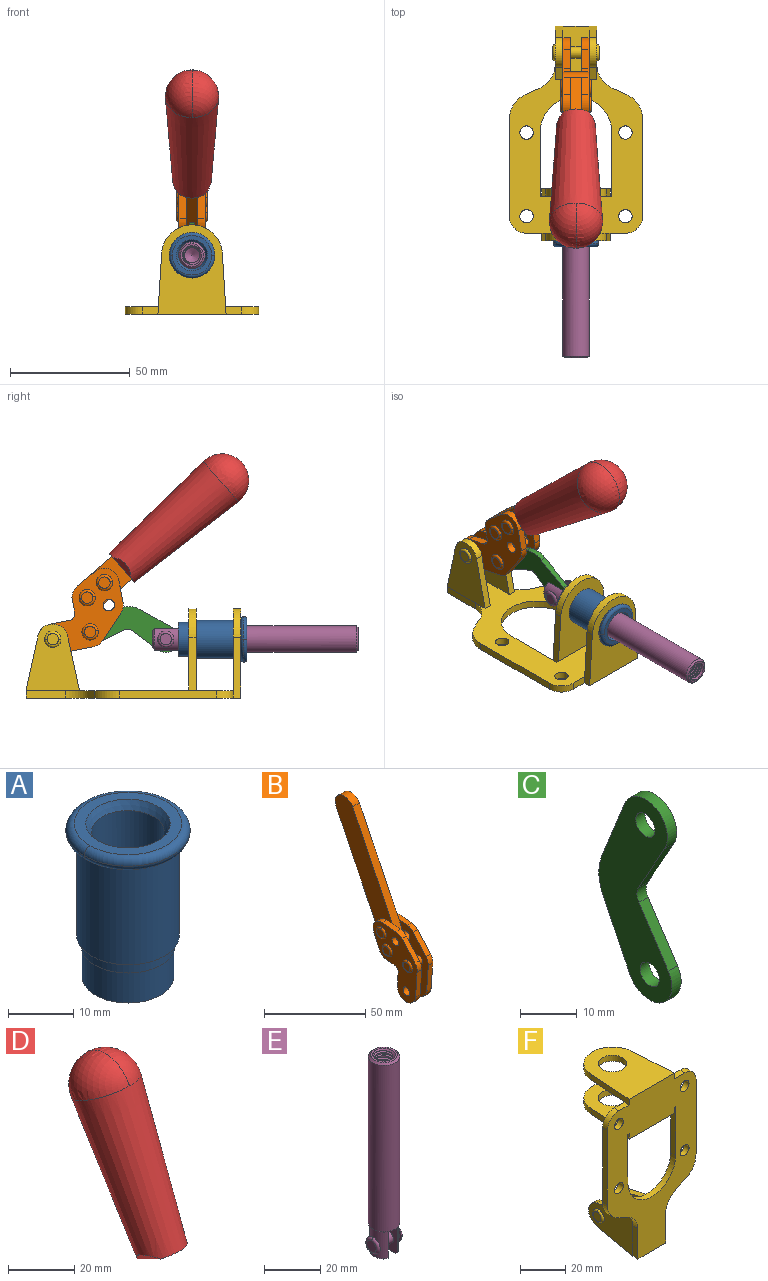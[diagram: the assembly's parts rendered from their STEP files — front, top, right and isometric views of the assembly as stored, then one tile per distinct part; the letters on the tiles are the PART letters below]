
ASSEMBLY  parts=6 mates=6
PART A: 15 faces, bbox 20.6x20.6x28.7 mm
  f0: torus R=8.26mm, axis (0,0,1), area 56.8mm2, adj f1,f10,f12
  f1: torus R=8.26mm, axis (0,0,1), area 56.8mm2, adj f0,f6,f13
  f2: cylinder r=5.59mm len=25.91mm, axis (0,0,1), area 909.6mm2, adj f3,f4
  f3: cone r=6.86mm half-angle=45deg, axis (0,0,-1), area 70.2mm2, adj f2,f14
  f4: cone r=6.47mm half-angle=30deg, axis (0,0,1), area 66.7mm2, adj f2,f13
  f5: cylinder r=7.04mm len=14.07mm, axis (0,0,1), area 252.6mm2, adj f11,f14
  f6: torus R=8.26mm, axis (0,0,1), area 56.8mm2, adj f1,f12,f13
  f7: cylinder r=7.16mm len=14.33mm, axis (0,0,1), area 91.5mm2, adj f9,f11
  f8: cylinder r=7.86mm len=18.42mm, axis (0,0,1), area 909.6mm2, adj f9,f10
  f9: plane 15.72x15.72mm, normal (0,0,-1), area 33mm2, adj f7,f8
  f10: plane 16.51x16.51mm, normal (0,0,-1), area 19.9mm2, adj f0,f8,f12
  f11: plane 14.33x14.33mm, normal (0,0,-1), area 5.7mm2, adj f5,f7
  f12: torus R=8.26mm, axis (0,0,1), area 56.8mm2, adj f0,f6,f10
  f13: plane 16.51x16.51mm, normal (0,0,1), area 82.7mm2, adj f1,f4,f6
  f14: plane 14.07x14.07mm, normal (0,0,-1), area 7.8mm2, adj f3,f5
PART B: 59 faces, bbox 12.9x60.2x99.6 mm
  f0: torus R=2.39mm, axis (-1,0,0), area 14.9mm2, adj f20,f43,f51
  f1: torus R=2.39mm, axis (-1,0,0), area 14.9mm2, adj f19,f42,f51
  f2: torus R=2.39mm, axis (-1,0,0), area 14.9mm2, adj f18,f35,f51
  f3: torus R=2.39mm, axis (-1,0,0), area 14.9mm2, adj f14,f17,f23
  f4: torus R=2.39mm, axis (-1,0,0), area 14.9mm2, adj f13,f16,f23
  f5: torus R=2.39mm, axis (-1,0,0), area 14.9mm2, adj f12,f15,f23
  f6: cylinder r=2.39mm len=4.78mm, axis (1,0,0), area 46.5mm2, adj f48,f50,f51
  f7: cylinder r=2.39mm len=4.78mm, axis (1,0,0), area 46.5mm2, adj f50,f51
  f8: cylinder r=6.35mm len=12.68mm, axis (1,0,0), area 61.8mm2, adj f38,f39,f50,f51
  f9: cylinder r=2.39mm len=4.78mm, axis (-1,0,0), area 70.5mm2, adj f46,f50
  f10: cylinder r=2.39mm len=4.78mm, axis (-1,0,0), area 46.5mm2, adj f23,f45,f46
  f11: cylinder r=2.39mm len=4.78mm, axis (-1,0,0), area 46.5mm2, adj f23,f46
  f12: plane 4.78x4.78mm, normal (1,0,0), area 17.9mm2, adj f5,f15
  f13: plane 4.78x4.78mm, normal (1,0,0), area 17.9mm2, adj f4,f16
  f14: plane 4.78x4.78mm, normal (1,0,0), area 17.9mm2, adj f3,f17
  f15: torus R=2.39mm, axis (-1,0,0), area 14.9mm2, adj f5,f12,f23
  f16: torus R=2.39mm, axis (-1,0,0), area 14.9mm2, adj f4,f13,f23
  f17: torus R=2.39mm, axis (-1,0,0), area 14.9mm2, adj f3,f14,f23
  f18: plane 4.78x4.78mm, normal (-1,0,0), area 17.9mm2, adj f2,f35
  f19: plane 4.78x4.78mm, normal (-1,0,0), area 17.9mm2, adj f1,f42
  f20: plane 4.78x4.78mm, normal (-1,0,0), area 17.9mm2, adj f0,f43
  f21: plane 2.26x0.2mm, normal (1,0,0), area 0.2mm2, adj f31,f44
  f22: plane 2.26x0.2mm, normal (-1,0,0), area 0.2mm2, adj f41,f44
  f23: plane 39.37x30.77mm, normal (1,0,0), area 565.5mm2, adj f3,f4,f5,f10,f11,f15,f16,f17
  f24: cylinder r=6.1mm len=4.15mm, axis (-1,0,0), area 14.7mm2, adj f23,f25,f32,f46
  f25: plane 10.25x9.01mm, normal (0,-0.75,0.66), area 42.3mm2, adj f23,f24,f26,f46
  f26: cylinder r=6.35mm len=4.64mm, axis (-1,0,0), area 15.6mm2, adj f23,f25,f27,f46
  f27: plane 15.84x3.1mm, normal (0,-1,-0.07), area 49.2mm2, adj f23,f26,f28,f46
  f28: cylinder r=6.35mm len=12.68mm, axis (-1,0,0), area 61.8mm2, adj f23,f27,f29,f46
  f29: plane 8.11x3.1mm, normal (0,1,0.07), area 25.2mm2, adj f23,f28,f30,f46
  f30: cylinder r=3.05mm len=3.25mm, axis (-1,0,0), area 14.8mm2, adj f23,f29,f31,f46
  f31: plane 5.99x3.1mm, normal (0,0.07,-1), area 18.6mm2, adj f21,f23,f30,f44,f46
  f32: plane 9.5x3.1mm, normal (0,-0.07,1), area 29.5mm2, adj f23,f24,f33,f46,f47
  f33: cylinder r=6.1mm len=8.63mm, axis (-1,0,0), area 39.1mm2, adj f23,f32,f34,f47
  f34: plane 8.65x3.96mm, normal (0,0.91,-0.42), area 29.5mm2, adj f23,f33,f44,f47
  f35: torus R=2.39mm, axis (-1,0,0), area 14.9mm2, adj f2,f18,f51
  f36: plane 10.25x9.01mm, normal (0,-0.75,0.66), area 42.3mm2, adj f37,f49,f50,f51
  f37: cylinder r=6.35mm len=4.64mm, axis (1,0,0), area 15.6mm2, adj f36,f38,f50,f51
  f38: plane 15.84x3.1mm, normal (0,-1,-0.07), area 49.2mm2, adj f8,f37,f50,f51
  f39: plane 8.11x3.1mm, normal (0,1,0.07), area 25.2mm2, adj f8,f40,f50,f51
  f40: cylinder r=3.05mm len=3.25mm, axis (1,0,0), area 14.8mm2, adj f39,f41,f50,f51
  f41: plane 5.99x3.1mm, normal (0,0.07,-1), area 18.6mm2, adj f22,f40,f44,f50,f51
  f42: torus R=2.39mm, axis (-1,0,0), area 14.9mm2, adj f1,f19,f51
  f43: torus R=2.39mm, axis (-1,0,0), area 14.9mm2, adj f0,f20,f51
  f44: cylinder r=6.35mm len=12.12mm, axis (-1,0,0), area 128.9mm2, adj f21,f22,f23,f31,f34,f41,f46,f47
  f45: plane 2.65x1.35mm, normal (1,0,0), area 1mm2, adj f10,f55
  f46: plane 39.08x20.42mm, normal (-1,0,0), area 412.5mm2, adj f9,f10,f11,f24,f25,f26,f27,f28
  f47: plane 77.62x39.82mm, normal (1,0,0), area 850mm2, adj f32,f33,f34,f44,f53,f54,f55
  f48: plane 2.65x1.35mm, normal (-1,0,0), area 1mm2, adj f6,f55
  f49: cylinder r=6.1mm len=4.15mm, axis (1,0,0), area 14.7mm2, adj f36,f50,f51,f56
  f50: plane 39.08x20.42mm, normal (1,0,0), area 412.5mm2, adj f6,f7,f8,f9,f36,f37,f38,f39
  f51: plane 39.37x30.77mm, normal (-1,0,0), area 565.5mm2, adj f0,f1,f2,f6,f7,f8,f35,f36
  f52: plane 8.65x3.96mm, normal (0,0.91,-0.42), area 29.5mm2, adj f44,f51,f57,f58
  f53: plane 68.49x33.4mm, normal (0,0.9,-0.44), area 358.1mm2, adj f44,f47,f54,f58
  f54: cylinder r=6.35mm len=12.06mm, axis (1,0,0), area 93.7mm2, adj f47,f53,f55,f58
  f55: plane 68.49x33.4mm, normal (0,-0.9,0.44), area 358.1mm2, adj f44,f45,f46,f47,f48,f50,f54,f58
  f56: plane 9.5x3.1mm, normal (0,-0.07,1), area 29.5mm2, adj f49,f50,f51,f57,f58
  f57: cylinder r=6.1mm len=8.63mm, axis (1,0,0), area 39.1mm2, adj f51,f52,f56,f58
  f58: plane 77.62x39.82mm, normal (-1,0,0), area 850mm2, adj f44,f52,f53,f54,f55,f56,f57
PART C: 12 faces, bbox 2.3x18.2x42.8 mm
  f0: cylinder r=2.4mm len=4.8mm, axis (1,0,0), area 34.9mm2, adj f4,f11
  f1: cylinder r=10.41mm len=8.47mm, axis (1,0,0), area 20.2mm2, adj f4,f9,f10,f11
  f2: cylinder r=3.05mm len=3.16mm, axis (1,0,0), area 7.7mm2, adj f4,f6,f7,f11
  f3: cylinder r=2.4mm len=4.8mm, axis (1,0,0), area 34.9mm2, adj f4,f11
  f4: plane 42.81x18.23mm, normal (-1,0,0), area 414.1mm2, adj f0,f1,f2,f3,f5,f6,f7,f8
  f5: cylinder r=5.54mm len=10.67mm, axis (1,0,0), area 41.8mm2, adj f4,f6,f10,f11
  f6: plane 11.66x6.53mm, normal (0,-0.87,-0.49), area 30.9mm2, adj f2,f4,f5,f11
  f7: plane 11.17x7.33mm, normal (0,-0.84,0.55), area 30.9mm2, adj f2,f4,f8,f11
  f8: cylinder r=5.54mm len=10.51mm, axis (1,0,0), area 41.8mm2, adj f4,f7,f9,f11
  f9: plane 13.67x6.67mm, normal (0,0.9,-0.44), area 35.1mm2, adj f1,f4,f8,f11
  f10: plane 14.1x5.7mm, normal (0,0.93,0.37), area 35.1mm2, adj f1,f4,f5,f11
  f11: plane 42.81x18.23mm, normal (1,0,0), area 414.1mm2, adj f0,f1,f2,f3,f5,f6,f7,f8
PART D: 11 faces, bbox 22.3x42.6x64.5 mm
  f0: sphere r=11.13mm, area 411.4mm2, adj f1,f8
  f1: cone r=11.11mm half-angle=3.3deg, axis (0,0.44,0.9), area 3251.8mm2, adj f0,f7,f8,f9,f10
  f2: cylinder r=6.16mm len=11.7mm, axis (1,0,0), area 89.5mm2, adj f3,f4,f5,f6
  f3: plane 60.23x36.75mm, normal (-1,0,0), area 763.6mm2, adj f2,f4,f6,f10
  f4: plane 51.37x25.05mm, normal (0,0.9,-0.44), area 264.2mm2, adj f2,f3,f5,f10
  f5: plane 60.23x36.75mm, normal (1,0,0), area 763.6mm2, adj f2,f4,f6,f10
  f6: plane 51.37x25.05mm, normal (0,-0.9,0.44), area 264.2mm2, adj f2,f3,f5,f10
  f7: plane 9.95x5.95mm, normal (0.71,-0.31,-0.64), area 25.8mm2, adj f1,f10
  f8: sphere r=11.13mm, area 411.4mm2, adj f0,f1
  f9: plane 9.95x5.95mm, normal (-0.71,-0.31,-0.64), area 25.8mm2, adj f1,f10
  f10: plane 14.27x11.38mm, normal (0,-0.44,-0.9), area 106.7mm2, adj f1,f3,f4,f5,f6,f7,f9
PART E: 48 faces, bbox 12.6x11.1x86.1 mm
  f0: torus R=2.41mm, axis (-1,0,0), area 15mm2, adj f30,f32,f34
  f1: torus R=2.41mm, axis (-1,0,0), area 15mm2, adj f29,f31,f33
  f2: cylinder r=5.54mm len=72.39mm, axis (0,0,1), area 2518.5mm2, adj f3,f4,f42,f43
  f3: cone r=5.54mm half-angle=45deg, axis (0,0,1), area 7.6mm2, adj f2,f5,f41
  f4: cone r=5.54mm half-angle=45deg, axis (0,0,-1), area 34.9mm2, adj f2,f39
  f5: cylinder r=5.08mm len=11.48mm, axis (0,0,1), area 108.3mm2, adj f3,f7,f8,f41
  f6: cylinder r=2.41mm len=4.83mm, axis (-1,0,0), area 71.2mm2, adj f40,f41
  f7: cylinder r=2.41mm len=4.83mm, axis (-1,0,0), area 7.6mm2, adj f5,f34
  f8: cone r=5.08mm half-angle=45deg, axis (0,0,1), area 10.6mm2, adj f5,f37,f41
  f9: cone r=3.98mm half-angle=45deg, axis (0,0,1), area 17.6mm2, adj f27,f39,f45,f46,f47
  f10: cylinder r=2.41mm len=4.83mm, axis (-1,0,0), area 7.6mm2, adj f33,f38
  f11: cylinder r=3.2mm len=6.4mm, axis (0,0,1), area 78.4mm2, adj f12,f28,f44,f45,f47
  f12: cylinder r=3.2mm len=6.4mm, axis (0,0,1), area 10.5mm2, adj f11,f13,f45,f47
  f13: cylinder r=3.2mm len=6.4mm, axis (0,0,1), area 10.5mm2, adj f12,f14,f45,f47
  f14: cylinder r=3.2mm len=6.4mm, axis (0,0,1), area 10.5mm2, adj f13,f15,f45,f47
  f15: cylinder r=3.2mm len=6.4mm, axis (0,0,1), area 10.5mm2, adj f14,f16,f45,f47
  f16: cylinder r=3.2mm len=6.4mm, axis (0,0,1), area 10.5mm2, adj f15,f17,f45,f47
  f17: cylinder r=3.2mm len=6.4mm, axis (0,0,1), area 10.5mm2, adj f16,f18,f45,f47
  f18: cylinder r=3.2mm len=6.4mm, axis (0,0,1), area 10.5mm2, adj f17,f19,f45,f47
  f19: cylinder r=3.2mm len=6.4mm, axis (0,0,1), area 10.5mm2, adj f18,f20,f45,f47
  f20: cylinder r=3.2mm len=6.4mm, axis (0,0,1), area 10.5mm2, adj f19,f21,f45,f47
  f21: cylinder r=3.2mm len=6.4mm, axis (0,0,1), area 10.5mm2, adj f20,f22,f45,f47
  f22: cylinder r=3.2mm len=6.4mm, axis (0,0,1), area 10.5mm2, adj f21,f23,f45,f47
  f23: cylinder r=3.2mm len=6.4mm, axis (0,0,1), area 10.5mm2, adj f22,f24,f45,f47
  f24: cylinder r=3.2mm len=6.4mm, axis (0,0,1), area 10.5mm2, adj f23,f25,f45,f47
  f25: cylinder r=3.2mm len=6.4mm, axis (0,0,1), area 10.5mm2, adj f24,f26,f45,f47
  f26: cylinder r=3.2mm len=6.4mm, axis (0,0,1), area 10.5mm2, adj f25,f27,f45,f47
  f27: cylinder r=3.2mm len=6.4mm, axis (0,0,1), area 7.4mm2, adj f9,f26,f45,f47
  f28: cone r=3.2mm half-angle=60deg, axis (0,0,1), area 37.2mm2, adj f11
  f29: plane 4.83x4.83mm, normal (-1,0,0), area 18.3mm2, adj f1,f31
  f30: plane 4.83x4.83mm, normal (1,0,0), area 18.3mm2, adj f0,f32
  f31: torus R=2.41mm, axis (-1,0,0), area 15mm2, adj f1,f29,f33
  f32: torus R=2.41mm, axis (-1,0,0), area 15mm2, adj f0,f30,f34
  f33: plane 6.83x6.83mm, normal (1,0,0), area 18.3mm2, adj f1,f10,f31
  f34: plane 6.83x6.83mm, normal (-1,0,0), area 18.3mm2, adj f0,f7,f32
  f35: cone r=5.08mm half-angle=45deg, axis (0,0,1), area 10.6mm2, adj f36,f38,f40
  f36: plane 7.25x1.97mm, normal (0,0,-1), area 10mm2, adj f35,f40
  f37: plane 7.25x1.97mm, normal (0,0,-1), area 10mm2, adj f8,f41
  f38: cylinder r=5.08mm len=11.48mm, axis (0,0,1), area 108.3mm2, adj f10,f35,f40,f42
  f39: plane 9.55x9.55mm, normal (0,0,1), area 22mm2, adj f4,f9
  f40: plane 12.76x10.09mm, normal (1,0,0), area 95.7mm2, adj f6,f35,f36,f38,f42,f43
  f41: plane 12.76x10.09mm, normal (-1,0,0), area 95.7mm2, adj f3,f5,f6,f8,f37,f43
  f42: cone r=5.54mm half-angle=45deg, axis (0,0,1), area 7.6mm2, adj f2,f38,f40
  f43: plane 11.07x4.7mm, normal (0,0,-1), area 50.4mm2, adj f2,f40,f41
  f44: plane 0.89x0.62mm, normal (-1,0,0), area 0.3mm2, adj f11,f45,f46,f47
  f45: bspline ~24.8x7.63mm, area 266.6mm2, adj f9,f11,f12,f13,f14,f15,f16,f17
  f46: bspline ~24.87x7.63mm, area 73.6mm2, adj f9,f44,f45,f47
  f47: bspline ~24.98x7.63mm, area 272.5mm2, adj f9,f11,f12,f13,f14,f15,f16,f17
PART F: 55 faces, bbox 55.7x37.4x89.8 mm
  f0: torus R=2.41mm, axis (-1,0,0), area 15mm2, adj f11,f15,f25
  f1: torus R=2.41mm, axis (-1,0,0), area 15mm2, adj f10,f12,f22
  f2: cylinder r=2.78mm len=5.56mm, axis (0,-1,0), area 54.2mm2, adj f30,f54
  f3: cylinder r=14.99mm len=29.97mm, axis (0,-1,0), area 145.9mm2, adj f30,f49,f53,f54
  f4: cylinder r=2.78mm len=5.56mm, axis (0,-1,0), area 54.2mm2, adj f30,f54
  f5: cylinder r=2.78mm len=5.56mm, axis (0,-1,0), area 54.2mm2, adj f30,f54
  f6: cylinder r=2.78mm len=5.56mm, axis (0,-1,0), area 54.2mm2, adj f30,f54
  f7: cylinder r=6.35mm len=12.7mm, axis (0,0,1), area 123.6mm2, adj f27,f51
  f8: cylinder r=6.35mm len=12.7mm, axis (0,0,-1), area 124.7mm2, adj f21,f35
  f9: cylinder r=2.41mm len=11.18mm, axis (-1,0,0), area 169.4mm2, adj f16,f19
  f10: plane 4.83x4.83mm, normal (1,0,0), area 18.3mm2, adj f1,f12
  f11: plane 4.83x4.83mm, normal (-1,0,0), area 18.3mm2, adj f0,f15
  f12: torus R=2.41mm, axis (-1,0,0), area 15mm2, adj f1,f10,f22
  f13: cylinder r=6.35mm len=12.41mm, axis (1,0,0), area 53.4mm2, adj f18,f19,f22,f23
  f14: cylinder r=6.35mm len=12.41mm, axis (-1,0,0), area 53.4mm2, adj f16,f17,f24,f25
  f15: torus R=2.41mm, axis (-1,0,0), area 15mm2, adj f0,f11,f25
  f16: plane 27.86x22.35mm, normal (1,0,0), area 425.4mm2, adj f9,f14,f17,f24,f30
  f17: plane 22.86x4.97mm, normal (0,0.21,0.98), area 72.5mm2, adj f14,f16,f25,f30
  f18: plane 22.86x4.97mm, normal (0,0.21,0.98), area 72.5mm2, adj f13,f19,f22,f30
  f19: plane 27.86x22.35mm, normal (-1,0,0), area 425.4mm2, adj f9,f13,f18,f23,f30
  f20: cylinder r=12.7mm len=25.35mm, axis (0,0,-1), area 119.8mm2, adj f21,f34,f35,f36
  f21: plane 34.21x28.07mm, normal (0,0,-1), area 702.4mm2, adj f8,f20,f30,f34,f36
  f22: plane 27.96x22.45mm, normal (1,0,0), area 407.2mm2, adj f1,f12,f13,f18,f23,f30,f42,f43
  f23: plane 22.86x4.97mm, normal (0,0.21,-0.98), area 72.5mm2, adj f13,f19,f22,f44
  f24: plane 22.86x4.97mm, normal (0,0.21,-0.98), area 72.5mm2, adj f14,f16,f25,f44
  f25: plane 27.86x22.35mm, normal (-1,0,0), area 407.1mm2, adj f0,f14,f15,f17,f24,f30,f45,f46
  f26: plane 3.1x0.95mm, normal (0,0,-1), area 2.7mm2, adj f30,f49,f50,f54
  f27: plane 34.21x28.07mm, normal (0,0,1), area 702.4mm2, adj f7,f28,f30,f50,f52
  f28: cylinder r=12.7mm len=25.35mm, axis (0,0,1), area 118.8mm2, adj f27,f50,f51,f52
  f29: plane 3.1x0.95mm, normal (0,0,-1), area 2.7mm2, adj f30,f52,f53,f54
  f30: plane 86.54x55.63mm, normal (0,1,0), area 2362.9mm2, adj f2,f3,f4,f5,f6,f16,f17,f18
  f31: plane 40.56x3.1mm, normal (-1,0,0), area 125.7mm2, adj f30,f32,f48,f54
  f32: cylinder r=7.11mm len=7.11mm, axis (0,-1,0), area 34.6mm2, adj f30,f31,f33,f54
  f33: plane 6.67x3.1mm, normal (0,0,1), area 20.4mm2, adj f30,f32,f34,f54
  f34: plane 25.39x3.13mm, normal (-1,0.06,0), area 79.5mm2, adj f20,f21,f33,f35,f54
  f35: plane 37.31x28.45mm, normal (0,0,1), area 789.9mm2, adj f8,f20,f34,f36,f54
  f36: plane 25.39x3.13mm, normal (1,0.06,0), area 79.5mm2, adj f20,f21,f35,f37,f54
  f37: plane 6.67x3.1mm, normal (0,0,1), area 20.4mm2, adj f30,f36,f38,f54
  f38: cylinder r=7.11mm len=7.11mm, axis (0,-1,0), area 34.6mm2, adj f30,f37,f39,f54
  f39: plane 40.56x3.1mm, normal (1,0,0), area 125.7mm2, adj f30,f38,f40,f54
  f40: cylinder r=11.18mm len=10.16mm, axis (0,-1,0), area 39.5mm2, adj f30,f39,f41,f54
  f41: plane 6.09x3.1mm, normal (0.42,0,-0.91), area 20.8mm2, adj f30,f40,f42,f54
  f42: cylinder r=11.18mm len=9.41mm, axis (0,-1,0), area 37.2mm2, adj f22,f30,f41,f43,f54
  f43: plane 16.5x3.1mm, normal (1,0,0), area 51.1mm2, adj f22,f42,f44,f54
  f44: plane 17.37x3.1mm, normal (0,0,-1), area 53.8mm2, adj f23,f24,f30,f43,f45,f54
  f45: plane 16.5x3.1mm, normal (-1,0,0), area 51.1mm2, adj f25,f44,f46,f54
  f46: cylinder r=11.18mm len=9.41mm, axis (0,-1,0), area 37.2mm2, adj f25,f30,f45,f47,f54
  f47: plane 6.09x3.1mm, normal (-0.42,0,-0.91), area 20.8mm2, adj f30,f46,f48,f54
  f48: cylinder r=11.18mm len=10.16mm, axis (0,-1,0), area 39.5mm2, adj f30,f31,f47,f54
  f49: plane 26.54x3.1mm, normal (-1,0,0), area 82.3mm2, adj f3,f26,f30,f54
  f50: plane 25.39x3.1mm, normal (1,0.06,0), area 78.8mm2, adj f26,f27,f28,f51,f54
  f51: plane 37.31x28.45mm, normal (0,0,-1), area 789.9mm2, adj f7,f28,f50,f52,f54
  f52: plane 25.39x3.1mm, normal (-1,0.06,0), area 78.8mm2, adj f27,f28,f29,f51,f54
  f53: plane 26.54x3.1mm, normal (1,0,0), area 82.3mm2, adj f3,f29,f30,f54
  f54: plane 89.66x55.63mm, normal (0,-1,0), area 2678.5mm2, adj f2,f3,f4,f5,f6,f26,f29,f31
PLACE A rot(axis=(1,0,0),90deg) t=(0,1.23,0)mm
PLACE B rot(axis=(1,0,0),75deg) t=(0,-4.04,9.14)mm
PLACE C rot(axis=(1,0,0),97.5deg) t=(0,4.68,2.22)mm
PLACE D rot(axis=(1,0,0),75deg) t=(0,-4.04,9.14)mm
PLACE E rot(axis=(1,0,0),90deg) t=(0,1.61,0)mm
PLACE F rot(axis=(1,0,0),90deg) t=(0,1.23,0)mm fixed
MATE revolute C.f3 <-> B.f4  axis (1,0,0) through (0,17.74,27.64)mm
MATE slider E.f2 <-> A.f2  axis (0,-1,0) through (0,-57.17,24.61)mm
MATE revolute C.f5 <-> E.f6  axis (1,0,0) through (0,-13.86,24.61)mm
MATE fastened D.f2 <-> B.f54  axis (1,0,0) through (0,-38.57,91.94)mm
MATE fastened A.f0 <-> F.f7  axis (0,1,0) through (0,-45.16,24.61)mm
MATE revolute B.f7 <-> F.f0  axis (1,0,0) through (0,33.32,24.61)mm
